# Revit family: kawneer-500_tuffline-sgl_no-tran-fr_20603
name_source: partatom
category: Doors
revit_build: Autodesk Revit 2015 (Build: 20140905_0730(x64)
units: mm (PartAtom-declared; Revit-internal decimal feet)

## types (1)
- kawneer-500_tuffline-sgl_no-tran-fr_20603
    2-Color Option = no
    Air Infiltration (ASTM E 283) = < 0.50 cfm/ft2  @ 6.24 psf (300 Pa), Single Doors
    Application = high traffic, high abuse
    Assembly Code = B2030110
    CSI Masterformat Code = 08 41 13
    Color = any
    Depth = 2"
    Description = The "500 Tuffline" wide stile heavy duty door offers durability in high abuse applications and is designed for  schools, universities, sports stadiums, and other high abuse areas.
    Door Corner Construction = Welded
    Door Handle Material = Aluminum - ASTM B 221 - 6063-T6 alloy and temper
    Door Opening = 28"
    Door Panel Height = 82"
    Door Panel Material = Aluminum - ASTM B 221 - 6063-T6 alloy and temper
    Door Panel Width = 28"
    Function = Interior
    Function (Interior or Exterior) = Exterior
    Glass Capture = Captured
    Glass Installtion = outside, inside
    Glass U-Factor = product not tested
    Glazing Thickness = 0"
    Height = 84"
    Hinging Types = Offset Pivot, Butt Hinge, Continuous Gear Hinge
    Keywords = Entrance, Door, Swing Door, Heavy Wall, Heavy Duty
    Manufacturer = Kawneer
    Manufacturer Part Number = 500 Tuffline® Entrance
    Model = 500 Tuffline® Entrance
    Overall U-Factor = product not tested
    Panel Inserts Material = Glass
    Product data url = https://bimobject.com
    Short Description = Wide Stile Heavy Duty Swing Door
    Sightline = 0"
    Type Comments = Wide Stile Heavy Duty Swing Door
    Type of Glazing = monolithic, insulating
    URL = http://www.kawneer.com
    Wall Closure = By host
    Water - Static (ASTM E 331) = product not tested
    Width = 32"

## geometry (parser evidence)
native form markers: Sweep x14
no freeform markers — native parametric forms only
